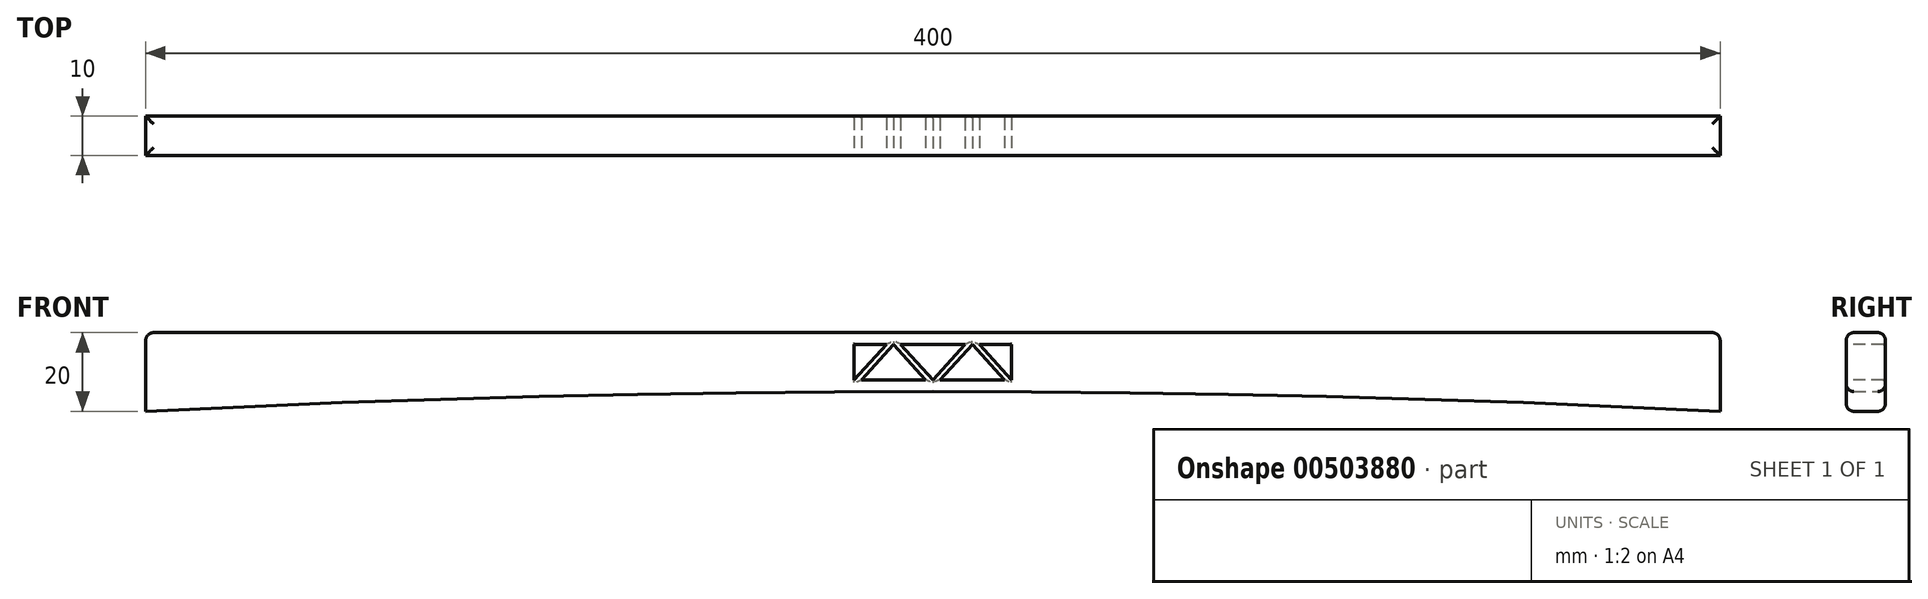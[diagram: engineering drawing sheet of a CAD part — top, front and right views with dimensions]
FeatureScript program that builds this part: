
annotation { "Feature Type Name" : "Feature", "Feature Type Description" : "" }
export const myFeature = defineFeature(function(context is Context, id is Id, definition is map)
    precondition{}
    {
        {
            var Q0;
            Q0=qCreatedBy(makeId("Front.planeOp"),FACE);
            var sketch = newSketch(context, id + "F0", { "sketchPlane" : qUnion([Q0])});
            skLineSegment(sketch, "E0.bottom", {"start": v(-200, 20) * mm, "end": v(200, 20) * mm});
            skLineSegment(sketch, "E0.left", {"start": v(-200, 20) * mm, "end": v(-200, 0) * mm});
            skLineSegment(sketch, "E0.right", {"start": v(200, 20) * mm, "end": v(200, 0) * mm});
            skPoint(sketch, "E1", {"position": v(0, -3980) * mm});
            skArc(sketch, "E2", {"start": v(200, 0) * mm, "mid": v(0, 5.02) * mm, "end": v(-200, 0) * mm});
            skSolve(sketch);
        }
        {
            var Q0;
            Q0=makeQuery(id+"F0.imprint","IMPRINT",FACE,{"disambiguationData":[TD([[makeQuery(id+"F0.imprint","IMPRINT",EDGE,{"derivedFrom":sQuery(id+"F0.wireOp",EDGE,"E0.bottom")}),-1.0]])]});
            extrude(context, id + "F1", {"entities" : qUnion([Q0]), "depth" : 10 * mm});
        }
        {
            var Q0;
            Q0=makeQuery(id+"F1.opExtrude","SWEPT_EDGE",EDGE,{"disambiguationData":[OSD([sQuery(id+"F0.wireOp",EDGE,"E0.bottom"),sQuery(id+"F0.wireOp",EDGE,"E0.right")])]});
            var Q1;
            Q1=makeQuery(id+"F1.opExtrude","CAP_EDGE",EDGE,{"disambiguationData":[OSD([sQuery(id+"F0.wireOp",EDGE,"E0.bottom")])],"isStart":true});
            var Q2;
            Q2=makeQuery(id+"F1.opExtrude","CAP_EDGE",EDGE,{"disambiguationData":[OSD([sQuery(id+"F0.wireOp",EDGE,"E0.bottom")])],"isStart":false});
            var Q3;
            Q3=makeQuery(id+"F1.opExtrude","SWEPT_EDGE",EDGE,{"disambiguationData":[OSD([sQuery(id+"F0.wireOp",EDGE,"E0.bottom"),sQuery(id+"F0.wireOp",EDGE,"E0.left")])]});
            fillet(context, id + "F2", {"entities" : qUnion([Q0, Q1, Q2, Q3]), "radius" : 2 * mm, "tangentPropagation" : true, "allowEdgeOverflow" : false});
        }
        {
            var Q0;
            Q0=makeQuery(id+"F1.opExtrude","CAP_EDGE",EDGE,{"disambiguationData":[OSD([sQuery(id+"F0.wireOp",EDGE,"E2")])],"isStart":false});
            fillet(context, id + "F3", {"entities" : qUnion([Q0]), "radius" : 2 * mm, "tangentPropagation" : true, "allowEdgeOverflow" : false});
        }
        {
            var Q0;
            Q0=makeQuery(id+"F1.opExtrude","CAP_EDGE",EDGE,{"disambiguationData":[OSD([sQuery(id+"F0.wireOp",EDGE,"E2")])],"isStart":true});
            fillet(context, id + "F4", {"entities" : qUnion([Q0]), "radius" : 2 * mm, "tangentPropagation" : true, "allowEdgeOverflow" : false});
        }
        {
            var Q0;
            Q0=makeQuery(id+"F1.opExtrude","CAP_FACE",FACE,{"disambiguationData":[OSD([sQuery(id+"F0.wireOp",EDGE,"E0.bottom"),sQuery(id+"F0.wireOp",EDGE,"E0.left"),sQuery(id+"F0.wireOp",EDGE,"E0.right"),sQuery(id+"F0.wireOp",EDGE,"E2")])],"isStart":false});
            var sketch = newSketch(context, id + "F5", { "sketchPlane" : qUnion([Q0])});
            skLineSegment(sketch, "E3", {"start": v(0, 7.02) * mm, "end": v(0, 18) * mm});
            skLineSegment(sketch, "E4", {"start": v(0, 18) * mm, "end": v(10, 18) * mm});
            skLineSegment(sketch, "E5", {"start": v(10, 18) * mm, "end": v(0, 7.02) * mm});
            skPoint(sketch, "E6", {"position": v(0, 17) * mm});
            skPoint(sketch, "E7", {"position": v(0, 8.02) * mm});
            skPoint(sketch, "E8", {"position": v(8.18, 17) * mm});
            skLineSegment(sketch, "E9", {"start": v(0, 17) * mm, "end": v(8.18, 17) * mm});
            skLineSegment(sketch, "E10", {"start": v(8.18, 17) * mm, "end": v(0, 8.02) * mm});
            skLineSegment(sketch, "E11", {"start": v(10, 18) * mm, "end": v(10, 7) * mm});
            skPoint(sketch, "E12", {"position": v(10, 17) * mm});
            skPoint(sketch, "E13", {"position": v(10, 8) * mm});
            skPoint(sketch, "E14", {"position": v(1.82, 8.02) * mm});
            skLineSegment(sketch, "E15", {"start": v(10, 17) * mm, "end": v(1.82, 8.02) * mm});
            skLineSegment(sketch, "E16", {"start": v(1.82, 8.02) * mm, "end": v(10, 8) * mm});
            skLineSegment(sketch, "E17.MirrorCS", {"start": v(10, 17) * mm, "end": v(18.18, 8.02) * mm});
            skLineSegment(sketch, "E18.MirrorCS", {"start": v(10, 18) * mm, "end": v(20, 7.02) * mm});
            skLineSegment(sketch, "E19.MirrorCS", {"start": v(18.18, 8.02) * mm, "end": v(10, 8) * mm});
            skLineSegment(sketch, "E20", {"start": v(20, 7.02) * mm, "end": v(20, 18) * mm});
            skPoint(sketch, "E21", {"position": v(20, 17) * mm});
            skPoint(sketch, "E22", {"position": v(20, 8.02) * mm});
            skPoint(sketch, "E23", {"position": v(11.82, 17) * mm});
            skLineSegment(sketch, "E24", {"start": v(20, 17) * mm, "end": v(11.82, 17) * mm});
            skLineSegment(sketch, "E25", {"start": v(11.82, 17) * mm, "end": v(20, 8.02) * mm});
            skLineSegment(sketch, "E26.MirrorCS", {"start": v(-10, 18) * mm, "end": v(-10, 7) * mm});
            skLineSegment(sketch, "E27.MirrorCS", {"start": v(-10, 17) * mm, "end": v(-18.18, 8.02) * mm});
            skLineSegment(sketch, "E28.MirrorCS", {"start": v(-18.18, 8.02) * mm, "end": v(-10, 8) * mm});
            skLineSegment(sketch, "E29.MirrorCS", {"start": v(-20, 17) * mm, "end": v(-11.82, 17) * mm});
            skLineSegment(sketch, "E30.MirrorCS", {"start": v(-10, 18) * mm, "end": v(0, 7.02) * mm});
            skLineSegment(sketch, "E31.MirrorCS", {"start": v(-8.18, 17) * mm, "end": v(0, 8.02) * mm});
            skLineSegment(sketch, "E32.MirrorCS", {"start": v(-1.82, 8.02) * mm, "end": v(-10, 8) * mm});
            skLineSegment(sketch, "E33.MirrorCS", {"start": v(-11.82, 17) * mm, "end": v(-20, 8.02) * mm});
            skLineSegment(sketch, "E34.MirrorCS", {"start": v(-10, 17) * mm, "end": v(-1.82, 8.02) * mm});
            skLineSegment(sketch, "E35.MirrorCS", {"start": v(-10, 18) * mm, "end": v(-20, 7.02) * mm});
            skLineSegment(sketch, "E36.MirrorCS", {"start": v(-20, 7.02) * mm, "end": v(-20, 18) * mm});
            skLineSegment(sketch, "E37.MirrorCS", {"start": v(0, 18) * mm, "end": v(-10, 18) * mm});
            skLineSegment(sketch, "E38.MirrorCS", {"start": v(0, 17) * mm, "end": v(-8.18, 17) * mm});
            skSolve(sketch);
        }
        {
            var Q0;
            {var subQ2=sQuery(id+"F5.wireOp",EDGE,"E31.MirrorCS");Q0=makeQuery(id+"F5.imprint","IMPRINT",FACE,{"disambiguationData":[TD([[makeQuery(id+"F5.imprint","IMPRINT",EDGE,{"derivedFrom":subQ2}),1.0]])]});}
            var Q1;
            {var subQ0=sQuery(id+"F5.wireOp",EDGE,"E9");Q1=makeQuery(id+"F5.imprint","IMPRINT",FACE,{"disambiguationData":[TD([[makeQuery(id+"F5.imprint","IMPRINT",EDGE,{"derivedFrom":subQ0}),-1.0]])]});}
            extrude(context, id + "F6", {"entities" : qUnion([Q0, Q1]), "operationType" : NewBodyOperationType.REMOVE, "endBound" : BoundingType.THROUGH_ALL, "oppositeDirection" : true, "depth" : 25 * mm});
        }
        {
            var Q0;
            {var subQ0=sQuery(id+"F5.wireOp",EDGE,"E27.MirrorCS");Q0=makeQuery(id+"F5.imprint","IMPRINT",FACE,{"disambiguationData":[TD([[makeQuery(id+"F5.imprint","IMPRINT",EDGE,{"derivedFrom":subQ0}),1.0]])]});}
            var Q1;
            {var subQ2=sQuery(id+"F5.wireOp",EDGE,"E32.MirrorCS");Q1=makeQuery(id+"F5.imprint","IMPRINT",FACE,{"disambiguationData":[TD([[makeQuery(id+"F5.imprint","IMPRINT",EDGE,{"derivedFrom":subQ2}),-1.0]])]});}
            extrude(context, id + "F7", {"entities" : qUnion([Q0, Q1]), "operationType" : NewBodyOperationType.REMOVE, "endBound" : BoundingType.THROUGH_ALL, "oppositeDirection" : true, "depth" : 25 * mm});
        }
        {
            var Q0;
            {var subQ0=sQuery(id+"F5.wireOp",EDGE,"E15");Q0=makeQuery(id+"F5.imprint","IMPRINT",FACE,{"disambiguationData":[TD([[makeQuery(id+"F5.imprint","IMPRINT",EDGE,{"derivedFrom":subQ0}),1.0]])]});}
            var Q1;
            {var subQ0=sQuery(id+"F5.wireOp",EDGE,"E17.MirrorCS");Q1=makeQuery(id+"F5.imprint","IMPRINT",FACE,{"disambiguationData":[TD([[makeQuery(id+"F5.imprint","IMPRINT",EDGE,{"derivedFrom":subQ0}),-1.0]])]});}
            extrude(context, id + "F8", {"entities" : qUnion([Q0, Q1]), "operationType" : NewBodyOperationType.REMOVE, "oppositeDirection" : true, "depth" : 25 * mm});
        }
        {
            var Q0;
            {var subQ0=sQuery(id+"F5.wireOp",EDGE,"E24");Q0=makeQuery(id+"F5.imprint","IMPRINT",FACE,{"disambiguationData":[TD([[makeQuery(id+"F5.imprint","IMPRINT",EDGE,{"derivedFrom":subQ0}),1.0]])]});}
            extrude(context, id + "F9", {"entities" : qUnion([Q0]), "operationType" : NewBodyOperationType.REMOVE, "oppositeDirection" : true, "depth" : 25 * mm});
        }
        {
            var Q0;
            {var subQ0=sQuery(id+"F5.wireOp",EDGE,"E29.MirrorCS");Q0=makeQuery(id+"F5.imprint","IMPRINT",FACE,{"disambiguationData":[TD([[makeQuery(id+"F5.imprint","IMPRINT",EDGE,{"derivedFrom":subQ0}),-1.0]])]});}
            extrude(context, id + "F10", {"entities" : qUnion([Q0]), "operationType" : NewBodyOperationType.REMOVE, "oppositeDirection" : true, "depth" : 25 * mm});
        }
        {
            var Q0;
            Q0=makeQuery(id+"F6.boolean.opBoolean","INTERSECT",EDGE,{"derivedFrom":[makeQuery(id+"F1.opExtrude","CAP_FACE",FACE,{"disambiguationData":[OSD([sQuery(id+"F0.wireOp",EDGE,"E0.bottom"),sQuery(id+"F0.wireOp",EDGE,"E0.left"),sQuery(id+"F0.wireOp",EDGE,"E0.right"),sQuery(id+"F0.wireOp",EDGE,"E2")])],"isStart":true}),makeQuery(id+"F6.opExtrude","SWEPT_FACE",FACE,{"disambiguationData":[OSD([sQuery(id+"F5.wireOp",EDGE,"E9"),sQuery(id+"F5.wireOp",EDGE,"E38.MirrorCS")])]})]});
            var Q1;
            Q1=makeQuery(id+"F6.boolean.opBoolean","COPY",EDGE,{"derivedFrom":makeQuery(id+"F6.opExtrude","CAP_EDGE",EDGE,{"disambiguationData":[OSD([sQuery(id+"F5.wireOp",EDGE,"E9"),sQuery(id+"F5.wireOp",EDGE,"E38.MirrorCS")])],"isStart":true})});
            fillet(context, id + "F11", {"entities" : qUnion([Q0, Q1]), "radius" : 0.62 * mm, "tangentPropagation" : true, "allowEdgeOverflow" : false});
        }
        {
            var Q0;
            Q0=makeQuery(id+"F8.boolean.opBoolean","INTERSECT",EDGE,{"derivedFrom":[makeQuery(id+"F1.opExtrude","CAP_FACE",FACE,{"disambiguationData":[OSD([sQuery(id+"F0.wireOp",EDGE,"E0.bottom"),sQuery(id+"F0.wireOp",EDGE,"E0.left"),sQuery(id+"F0.wireOp",EDGE,"E0.right"),sQuery(id+"F0.wireOp",EDGE,"E2")])],"isStart":true}),makeQuery(id+"F8.opExtrude","SWEPT_FACE",FACE,{"disambiguationData":[OSD([sQuery(id+"F5.wireOp",EDGE,"E15")])]})]});
            var Q1;
            Q1=makeQuery(id+"F8.boolean.opBoolean","COPY",EDGE,{"derivedFrom":makeQuery(id+"F8.opExtrude","CAP_EDGE",EDGE,{"disambiguationData":[OSD([sQuery(id+"F5.wireOp",EDGE,"E15")])],"isStart":true})});
            fillet(context, id + "F12", {"entities" : qUnion([Q0, Q1]), "radius" : 0.62 * mm, "tangentPropagation" : true, "allowEdgeOverflow" : false});
        }
        {
            var Q0;
            Q0=makeQuery(id+"F8.boolean.opBoolean","INTERSECT",EDGE,{"derivedFrom":[makeQuery(id+"F1.opExtrude","CAP_FACE",FACE,{"disambiguationData":[OSD([sQuery(id+"F0.wireOp",EDGE,"E0.bottom"),sQuery(id+"F0.wireOp",EDGE,"E0.left"),sQuery(id+"F0.wireOp",EDGE,"E0.right"),sQuery(id+"F0.wireOp",EDGE,"E2")])],"isStart":true}),makeQuery(id+"F8.opExtrude","SWEPT_FACE",FACE,{"disambiguationData":[OSD([sQuery(id+"F5.wireOp",EDGE,"E17.MirrorCS")])]})]});
            var Q1;
            Q1=makeQuery(id+"F8.boolean.opBoolean","COPY",EDGE,{"derivedFrom":makeQuery(id+"F8.opExtrude","CAP_EDGE",EDGE,{"disambiguationData":[OSD([sQuery(id+"F5.wireOp",EDGE,"E17.MirrorCS")])],"isStart":true})});
            fillet(context, id + "F13", {"entities" : qUnion([Q0, Q1]), "radius" : 0.5 * mm, "tangentPropagation" : true, "allowEdgeOverflow" : false});
        }
        {
            var Q0;
            Q0=makeQuery(id+"F6.boolean.opBoolean","INTERSECT",EDGE,{"derivedFrom":[makeQuery(id+"F1.opExtrude","CAP_FACE",FACE,{"disambiguationData":[OSD([sQuery(id+"F0.wireOp",EDGE,"E0.bottom"),sQuery(id+"F0.wireOp",EDGE,"E0.left"),sQuery(id+"F0.wireOp",EDGE,"E0.right"),sQuery(id+"F0.wireOp",EDGE,"E2")])],"isStart":true}),makeQuery(id+"F6.opExtrude","SWEPT_FACE",FACE,{"disambiguationData":[OSD([sQuery(id+"F5.wireOp",EDGE,"E10")])]})]});
            var Q1;
            Q1=makeQuery(id+"F6.boolean.opBoolean","COPY",EDGE,{"derivedFrom":makeQuery(id+"F6.opExtrude","CAP_EDGE",EDGE,{"disambiguationData":[OSD([sQuery(id+"F5.wireOp",EDGE,"E10")])],"isStart":true})});
            fillet(context, id + "F14", {"entities" : qUnion([Q0, Q1]), "radius" : 0.62 * mm, "tangentPropagation" : true, "allowEdgeOverflow" : false});
        }
        {
            var Q0;
            Q0=makeQuery(id+"F6.boolean.opBoolean","COPY",EDGE,{"derivedFrom":makeQuery(id+"F6.opExtrude","CAP_EDGE",EDGE,{"disambiguationData":[OSD([sQuery(id+"F5.wireOp",EDGE,"E31.MirrorCS")])],"isStart":true})});
            var Q1;
            Q1=makeQuery(id+"F6.boolean.opBoolean","INTERSECT",EDGE,{"derivedFrom":[makeQuery(id+"F1.opExtrude","CAP_FACE",FACE,{"disambiguationData":[OSD([sQuery(id+"F0.wireOp",EDGE,"E0.bottom"),sQuery(id+"F0.wireOp",EDGE,"E0.left"),sQuery(id+"F0.wireOp",EDGE,"E0.right"),sQuery(id+"F0.wireOp",EDGE,"E2")])],"isStart":true}),makeQuery(id+"F6.opExtrude","SWEPT_FACE",FACE,{"disambiguationData":[OSD([sQuery(id+"F5.wireOp",EDGE,"E31.MirrorCS")])]})]});
            fillet(context, id + "F15", {"entities" : qUnion([Q0, Q1]), "radius" : 0.5 * mm, "tangentPropagation" : true, "allowEdgeOverflow" : false});
        }
        {
            var Q0;
            Q0=makeQuery(id+"F8.boolean.opBoolean","INTERSECT",EDGE,{"derivedFrom":[makeQuery(id+"F1.opExtrude","CAP_FACE",FACE,{"disambiguationData":[OSD([sQuery(id+"F0.wireOp",EDGE,"E0.bottom"),sQuery(id+"F0.wireOp",EDGE,"E0.left"),sQuery(id+"F0.wireOp",EDGE,"E0.right"),sQuery(id+"F0.wireOp",EDGE,"E2")])],"isStart":true}),makeQuery(id+"F8.opExtrude","SWEPT_FACE",FACE,{"disambiguationData":[OSD([sQuery(id+"F5.wireOp",EDGE,"E16")])]})]});
            var Q1;
            Q1=makeQuery(id+"F8.boolean.opBoolean","COPY",EDGE,{"derivedFrom":makeQuery(id+"F8.opExtrude","CAP_EDGE",EDGE,{"disambiguationData":[OSD([sQuery(id+"F5.wireOp",EDGE,"E16")])],"isStart":true})});
            var Q2;
            Q2=makeQuery(id+"F8.boolean.opBoolean","INTERSECT",EDGE,{"derivedFrom":[makeQuery(id+"F1.opExtrude","CAP_FACE",FACE,{"disambiguationData":[OSD([sQuery(id+"F0.wireOp",EDGE,"E0.bottom"),sQuery(id+"F0.wireOp",EDGE,"E0.left"),sQuery(id+"F0.wireOp",EDGE,"E0.right"),sQuery(id+"F0.wireOp",EDGE,"E2")])],"isStart":true}),makeQuery(id+"F8.opExtrude","SWEPT_FACE",FACE,{"disambiguationData":[OSD([sQuery(id+"F5.wireOp",EDGE,"E19.MirrorCS")])]})]});
            var Q3;
            Q3=makeQuery(id+"F8.boolean.opBoolean","COPY",EDGE,{"derivedFrom":makeQuery(id+"F8.opExtrude","CAP_EDGE",EDGE,{"disambiguationData":[OSD([sQuery(id+"F5.wireOp",EDGE,"E19.MirrorCS")])],"isStart":true})});
            fillet(context, id + "F16", {"entities" : qUnion([Q0, Q1, Q2, Q3]), "radius" : 0.5 * mm, "tangentPropagation" : true, "allowEdgeOverflow" : false});
        }
        {
            var Q0;
            Q0=makeQuery(id+"F9.boolean.opBoolean","COPY",EDGE,{"derivedFrom":makeQuery(id+"F9.opExtrude","CAP_EDGE",EDGE,{"disambiguationData":[OSD([sQuery(id+"F5.wireOp",EDGE,"E25")])],"isStart":true})});
            var Q1;
            Q1=makeQuery(id+"F9.boolean.opBoolean","INTERSECT",EDGE,{"derivedFrom":[makeQuery(id+"F1.opExtrude","CAP_FACE",FACE,{"disambiguationData":[OSD([sQuery(id+"F0.wireOp",EDGE,"E0.bottom"),sQuery(id+"F0.wireOp",EDGE,"E0.left"),sQuery(id+"F0.wireOp",EDGE,"E0.right"),sQuery(id+"F0.wireOp",EDGE,"E2")])],"isStart":true}),makeQuery(id+"F9.opExtrude","SWEPT_FACE",FACE,{"disambiguationData":[OSD([sQuery(id+"F5.wireOp",EDGE,"E25")])]})]});
            fillet(context, id + "F17", {"entities" : qUnion([Q0, Q1]), "radius" : 0.5 * mm, "tangentPropagation" : true, "allowEdgeOverflow" : false});
        }
        {
            var Q0;
            Q0=makeQuery(id+"F9.boolean.opBoolean","INTERSECT",EDGE,{"derivedFrom":[makeQuery(id+"F1.opExtrude","CAP_FACE",FACE,{"disambiguationData":[OSD([sQuery(id+"F0.wireOp",EDGE,"E0.bottom"),sQuery(id+"F0.wireOp",EDGE,"E0.left"),sQuery(id+"F0.wireOp",EDGE,"E0.right"),sQuery(id+"F0.wireOp",EDGE,"E2")])],"isStart":true}),makeQuery(id+"F9.opExtrude","SWEPT_FACE",FACE,{"disambiguationData":[OSD([sQuery(id+"F5.wireOp",EDGE,"E24")])]})]});
            var Q1;
            Q1=makeQuery(id+"F9.boolean.opBoolean","COPY",EDGE,{"derivedFrom":makeQuery(id+"F9.opExtrude","CAP_EDGE",EDGE,{"disambiguationData":[OSD([sQuery(id+"F5.wireOp",EDGE,"E24")])],"isStart":true})});
            fillet(context, id + "F18", {"entities" : qUnion([Q0, Q1]), "radius" : 0.5 * mm, "tangentPropagation" : true, "allowEdgeOverflow" : false});
        }
        {
            var Q0;
            Q0=makeQuery(id+"F7.boolean.opBoolean","COPY",EDGE,{"derivedFrom":makeQuery(id+"F7.opExtrude","CAP_EDGE",EDGE,{"disambiguationData":[OSD([sQuery(id+"F5.wireOp",EDGE,"E28.MirrorCS")])],"isStart":true})});
            var Q1;
            Q1=makeQuery(id+"F7.boolean.opBoolean","COPY",EDGE,{"derivedFrom":makeQuery(id+"F7.opExtrude","CAP_EDGE",EDGE,{"disambiguationData":[OSD([sQuery(id+"F5.wireOp",EDGE,"E32.MirrorCS")])],"isStart":true})});
            var Q2;
            Q2=makeQuery(id+"F7.boolean.opBoolean","INTERSECT",EDGE,{"derivedFrom":[makeQuery(id+"F1.opExtrude","CAP_FACE",FACE,{"disambiguationData":[OSD([sQuery(id+"F0.wireOp",EDGE,"E0.bottom"),sQuery(id+"F0.wireOp",EDGE,"E0.left"),sQuery(id+"F0.wireOp",EDGE,"E0.right"),sQuery(id+"F0.wireOp",EDGE,"E2")])],"isStart":true}),makeQuery(id+"F7.opExtrude","SWEPT_FACE",FACE,{"disambiguationData":[OSD([sQuery(id+"F5.wireOp",EDGE,"E28.MirrorCS")])]})]});
            var Q3;
            Q3=makeQuery(id+"F7.boolean.opBoolean","INTERSECT",EDGE,{"derivedFrom":[makeQuery(id+"F1.opExtrude","CAP_FACE",FACE,{"disambiguationData":[OSD([sQuery(id+"F0.wireOp",EDGE,"E0.bottom"),sQuery(id+"F0.wireOp",EDGE,"E0.left"),sQuery(id+"F0.wireOp",EDGE,"E0.right"),sQuery(id+"F0.wireOp",EDGE,"E2")])],"isStart":true}),makeQuery(id+"F7.opExtrude","SWEPT_FACE",FACE,{"disambiguationData":[OSD([sQuery(id+"F5.wireOp",EDGE,"E27.MirrorCS")])]})]});
            var Q4;
            Q4=makeQuery(id+"F7.boolean.opBoolean","COPY",EDGE,{"derivedFrom":makeQuery(id+"F7.opExtrude","CAP_EDGE",EDGE,{"disambiguationData":[OSD([sQuery(id+"F5.wireOp",EDGE,"E34.MirrorCS")])],"isStart":true})});
            var Q5;
            Q5=makeQuery(id+"F10.boolean.opBoolean","INTERSECT",EDGE,{"derivedFrom":[makeQuery(id+"F1.opExtrude","CAP_FACE",FACE,{"disambiguationData":[OSD([sQuery(id+"F0.wireOp",EDGE,"E0.bottom"),sQuery(id+"F0.wireOp",EDGE,"E0.left"),sQuery(id+"F0.wireOp",EDGE,"E0.right"),sQuery(id+"F0.wireOp",EDGE,"E2")])],"isStart":true}),makeQuery(id+"F10.opExtrude","SWEPT_FACE",FACE,{"disambiguationData":[OSD([sQuery(id+"F5.wireOp",EDGE,"E33.MirrorCS")])]})]});
            var Q6;
            Q6=makeQuery(id+"F7.boolean.opBoolean","COPY",EDGE,{"derivedFrom":makeQuery(id+"F7.opExtrude","CAP_EDGE",EDGE,{"disambiguationData":[OSD([sQuery(id+"F5.wireOp",EDGE,"E27.MirrorCS")])],"isStart":true})});
            var Q7;
            Q7=makeQuery(id+"F10.boolean.opBoolean","COPY",EDGE,{"derivedFrom":makeQuery(id+"F10.opExtrude","CAP_EDGE",EDGE,{"disambiguationData":[OSD([sQuery(id+"F5.wireOp",EDGE,"E33.MirrorCS")])],"isStart":true})});
            var Q8;
            Q8=makeQuery(id+"F7.boolean.opBoolean","INTERSECT",EDGE,{"derivedFrom":[makeQuery(id+"F1.opExtrude","CAP_FACE",FACE,{"disambiguationData":[OSD([sQuery(id+"F0.wireOp",EDGE,"E0.bottom"),sQuery(id+"F0.wireOp",EDGE,"E0.left"),sQuery(id+"F0.wireOp",EDGE,"E0.right"),sQuery(id+"F0.wireOp",EDGE,"E2")])],"isStart":true}),makeQuery(id+"F7.opExtrude","SWEPT_FACE",FACE,{"disambiguationData":[OSD([sQuery(id+"F5.wireOp",EDGE,"E32.MirrorCS")])]})]});
            var Q9;
            Q9=makeQuery(id+"F7.boolean.opBoolean","INTERSECT",EDGE,{"derivedFrom":[makeQuery(id+"F1.opExtrude","CAP_FACE",FACE,{"disambiguationData":[OSD([sQuery(id+"F0.wireOp",EDGE,"E0.bottom"),sQuery(id+"F0.wireOp",EDGE,"E0.left"),sQuery(id+"F0.wireOp",EDGE,"E0.right"),sQuery(id+"F0.wireOp",EDGE,"E2")])],"isStart":true}),makeQuery(id+"F7.opExtrude","SWEPT_FACE",FACE,{"disambiguationData":[OSD([sQuery(id+"F5.wireOp",EDGE,"E34.MirrorCS")])]})]});
            fillet(context, id + "F19", {"entities" : qUnion([Q0, Q1, Q2, Q3, Q4, Q5, Q6, Q7, Q8, Q9]), "radius" : 0.5 * mm, "tangentPropagation" : true, "allowEdgeOverflow" : false});
        }
        {
            var Q0;
            Q0=makeQuery(id+"F10.boolean.opBoolean","COPY",EDGE,{"derivedFrom":makeQuery(id+"F10.opExtrude","CAP_EDGE",EDGE,{"disambiguationData":[OSD([sQuery(id+"F5.wireOp",EDGE,"E29.MirrorCS")])],"isStart":true})});
            var Q1;
            Q1=makeQuery(id+"F10.boolean.opBoolean","INTERSECT",EDGE,{"derivedFrom":[makeQuery(id+"F1.opExtrude","CAP_FACE",FACE,{"disambiguationData":[OSD([sQuery(id+"F0.wireOp",EDGE,"E0.bottom"),sQuery(id+"F0.wireOp",EDGE,"E0.left"),sQuery(id+"F0.wireOp",EDGE,"E0.right"),sQuery(id+"F0.wireOp",EDGE,"E2")])],"isStart":true}),makeQuery(id+"F10.opExtrude","SWEPT_FACE",FACE,{"disambiguationData":[OSD([sQuery(id+"F5.wireOp",EDGE,"E29.MirrorCS")])]})]});
            fillet(context, id + "F20", {"entities" : qUnion([Q0, Q1]), "radius" : 0.5 * mm, "tangentPropagation" : true, "allowEdgeOverflow" : false});
        }
    });
